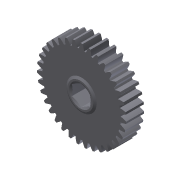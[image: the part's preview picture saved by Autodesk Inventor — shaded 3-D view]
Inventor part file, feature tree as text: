
AUTODESK INVENTOR PART (.ipt)
format: ipt  version: 2011 (Build 150239000, 239)  size: 322,048 bytes
history: native  units: mm (DEFAULTED — no unit token found)
features: sketch x5, other x4, extrude x3, plane x3, revolve x1, projected_geometry x1
ambient origin geometry x8: Origin, YZ Plane, XZ Plane, XY Plane, X Axis, Y Axis, Z Axis, Center Point
bodies: Solid1 (feature_tree)
feature tree (17):
  other  "Gear 35T 20dp 375hex"
  extrude  "Extrusion1"  Depth=9.525mm TaperAngle=0.0deg
  plane  "Work Plane1"
  plane  "Work Plane2"
  plane  "Work Plane3"
  other  "Spur Gear"
  extrude  "Extrusion2"  Depth=76.2mm TaperAngle=0.0deg
  extrude  "Extrusion3"  TaperAngle=0.0deg  [1 undecoded]
  revolve  "Revolution1"  [1 undecoded]
  sketch  "Sketch1"  dims[d0=46.99mm d1=9.525mm d2=0.0mm]
  sketch  "Sketch2"  dims[d3=44.45mm d4=76.2mm d5=0.0mm]
  other  "Srf1"
  sketch  "Sketch3"  dims[d6=0.0mm d7=0.897598mm d9=0.0mm]
  sketch  "Sketch4"  dims[d14=0.0mm d15=111.125mm d16=0.0mm]
  sketch  "Sketch5"  dims[d17=0.0mm d18=0.0mm d19=111.125mm d20=15.9004mm d21=0.635mm d22=0.0mm d23=9.525mm d24=0.635mm d25=0.0mm d26=1.143mm d27=0.889mm d28=5.070181mm d29=2.54mm d30=90.0deg]
  other  "Pitch Diameter"
  projected_geometry  "Project Cut Edges1"
note: 2 required parameter values undecoded (feature->parameter linkage not recoverable at this tier; creation-order binding heuristic only, values carry confidence <= 0.55)